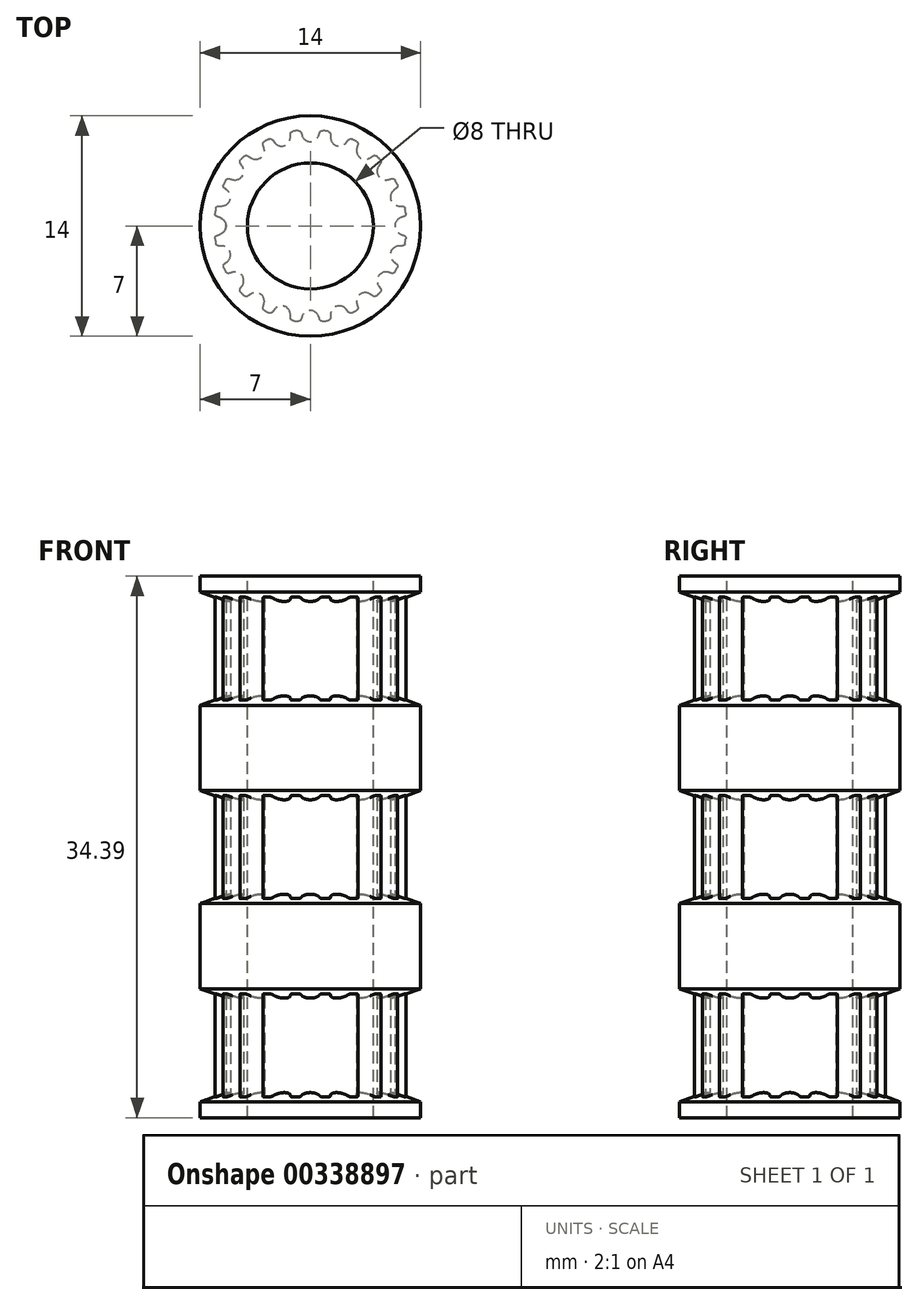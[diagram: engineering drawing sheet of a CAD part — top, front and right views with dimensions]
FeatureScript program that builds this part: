
annotation { "Feature Type Name" : "Feature", "Feature Type Description" : "" }
export const myFeature = defineFeature(function(context is Context, id is Id, definition is map)
    precondition{}
    {
        {
            assignVariable(context, id + "F0", {"name" : "teeth", "anyValue" : 20});
        }
        {
            assignVariable(context, id + "F1", {"name" : "total_length", "anyValue" : 34});
        }
        {
            var Q0;
            Q0=qCreatedBy(makeId("Top.planeOp"),FACE);
            var sketch = newSketch(context, id + "F2", { "sketchPlane" : qUnion([Q0])});
            skLineSegment(sketch, "E0", {"start": v(0, 0) * mm, "end": v(0, 5.36) * mm, "construction": true});
            skCircle(sketch, "E1", {"center": v(0, 0) * mm, "radius": 6.11 * mm});
            skPoint(sketch, "E2.MirrorCS.end.orphan", {"position": v(0.96, 6.04) * mm});
            skLineSegment(sketch, "E3", {"start": v(0.96, 6.04) * mm, "end": v(1, 6.29) * mm, "construction": true});
            skLineSegment(sketch, "E4", {"start": v(-0.96, 6.04) * mm, "end": v(-1, 6.29) * mm, "construction": true});
            skArc(sketch, "E5", {"start": v(0, 5.36) * mm, "mid": v(0.31, 5.46) * mm, "end": v(0.52, 5.72) * mm});
            skArc(sketch, "E6", {"start": v(0.52, 5.72) * mm, "mid": v(0.56, 5.83) * mm, "end": v(0.58, 5.94) * mm, "construction": true});
            skLineSegment(sketch, "E7", {"start": v(0, 5.36) * mm, "end": v(0, 6.11) * mm, "construction": true});
            skLineSegment(sketch, "E8", {"start": v(0, 6.11) * mm, "end": v(0, 6.37) * mm, "construction": true});
            skArc(sketch, "E9", {"start": v(0.58, 5.94) * mm, "mid": v(0.64, 6.04) * mm, "end": v(0.75, 6.07) * mm, "construction": true});
            skArc(sketch, "E10", {"start": v(1, 6.29) * mm, "mid": v(0, 6.37) * mm, "end": v(-1, 6.29) * mm, "construction": true});
            skLineSegment(sketch, "E11", {"start": v(0.96, 6.04) * mm, "end": v(0.84, 5.3) * mm});
            skLineSegment(sketch, "E12", {"start": v(0.84, 5.3) * mm, "end": v(0, 0) * mm});
            skLineSegment(sketch, "E13", {"start": v(0, 0) * mm, "end": v(-0.84, 5.3) * mm});
            skLineSegment(sketch, "E14", {"start": v(-0.84, 5.3) * mm, "end": v(-0.96, 6.04) * mm});
            skArc(sketch, "E15", {"start": v(0.8, 6.06) * mm, "mid": v(0.67, 6.03) * mm, "end": v(0.6, 5.93) * mm});
            skArc(sketch, "E16", {"start": v(0.52, 5.72) * mm, "mid": v(0.56, 5.83) * mm, "end": v(0.6, 5.93) * mm});
            skArc(sketch, "E17.MirrorCS", {"start": v(0, 5.36) * mm, "mid": v(-0.31, 5.46) * mm, "end": v(-0.52, 5.72) * mm});
            skArc(sketch, "E18.MirrorCS", {"start": v(-0.52, 5.72) * mm, "mid": v(-0.56, 5.83) * mm, "end": v(-0.6, 5.93) * mm});
            skArc(sketch, "E19.MirrorCS", {"start": v(-0.8, 6.06) * mm, "mid": v(-0.67, 6.03) * mm, "end": v(-0.6, 5.93) * mm});
            skArc(sketch, "E20", {"start": v(0, 6.11) * mm, "mid": v(-0.2, 6.1) * mm, "end": v(-0.4, 6.1) * mm});
            skArc(sketch, "E21", {"start": v(0.84, 5.3) * mm, "mid": v(0, 5.36) * mm, "end": v(-0.84, 5.3) * mm, "construction": true});
            skLineSegment(sketch, "E22", {"start": v(1, 6.29) * mm, "end": v(1.05, 6.66) * mm, "construction": true});
            skLineSegment(sketch, "E23", {"start": v(-1, 6.29) * mm, "end": v(-1.05, 6.66) * mm, "construction": true});
            skArc(sketch, "E24", {"start": v(-1.05, 6.66) * mm, "mid": v(0, 6.74) * mm, "end": v(1.05, 6.66) * mm, "construction": true});
            skSolve(sketch);
        }
        {
            var Q0;
            Q0=makeQuery(id+"F2.imprint","IMPRINT",FACE,{"disambiguationData":[TD([[makeQuery(id+"F2.imprint","IMPRINT",EDGE,{"derivedFrom":sQuery(id+"F2.wireOp",EDGE,"E5")}),-1.0]])]});
            var Q1;
            {var subQ1=sQuery(id+"F2.wireOp",EDGE,"E14");Q1=makeQuery(id+"F2.imprint","IMPRINT",FACE,{"disambiguationData":[TD([[makeQuery(id+"F2.imprint","IMPRINT",EDGE,{"derivedFrom":subQ1}),-1.0]])]});}
            var Q2;
            {var subQ0=sQuery(id+"F2.wireOp",EDGE,"E12");Q2=makeQuery(id+"F2.imprint","IMPRINT",FACE,{"disambiguationData":[TD([[makeQuery(id+"F2.imprint","IMPRINT",EDGE,{"derivedFrom":subQ0}),-1.0]])]});}
            extrude(context, id + "F3", {"entities" : qUnion([Q0, Q1, Q2]), "endBound" : BoundingType.SYMMETRIC, "depth" : (getVariable(context, 'total_length')) * mm});
        }
        {
            var Q0;
            Q0=makeQuery(id+"F3.opExtrude","SWEPT_BODY",BODY,{"disambiguationData":[OSD([sQuery(id+"F2.wireOp",EDGE,"E1"),sQuery(id+"F2.wireOp",EDGE,"E5"),sQuery(id+"F2.wireOp",EDGE,"E11"),sQuery(id+"F2.wireOp",EDGE,"E12"),sQuery(id+"F2.wireOp",EDGE,"E13"),sQuery(id+"F2.wireOp",EDGE,"E14"),sQuery(id+"F2.wireOp",EDGE,"E15"),sQuery(id+"F2.wireOp",EDGE,"E16"),sQuery(id+"F2.wireOp",EDGE,"E17.MirrorCS"),sQuery(id+"F2.wireOp",EDGE,"E18.MirrorCS"),sQuery(id+"F2.wireOp",EDGE,"E19.MirrorCS")])]});
            var Q1;
            Q1=makeQuery(id+"F3.opExtrude","SWEPT_EDGE",EDGE,{"disambiguationData":[OSD([sQuery(id+"F2.wireOp",EDGE,"E12"),sQuery(id+"F2.wireOp",EDGE,"E13")])]});
            circularPattern(context, id + "F4", {"operationType" : NewBodyOperationType.ADD, "entities" : qUnion([Q0]), "axis" : qUnion([Q1]), "angle" : 360 * degree, "instanceCount" : getVariable(context, 'teeth'), "equalSpace" : true});
        }
        {
            var Q0;
            Q0=qCreatedBy(makeId("Front.planeOp"),FACE);
            var sketch = newSketch(context, id + "F5", { "sketchPlane" : qUnion([Q0])});
            skLineSegment(sketch, "E25", {"start": v(0, 17) * mm, "end": v(7, 17) * mm});
            skLineSegment(sketch, "E26", {"start": v(7, 17) * mm, "end": v(7, 16) * mm});
            skLineSegment(sketch, "E27", {"start": v(7, 16) * mm, "end": v(5.36, 15.4) * mm});
            skLineSegment(sketch, "E28", {"start": v(5.36, 15.4) * mm, "end": v(0, 15.4) * mm});
            skLineSegment(sketch, "E29", {"start": v(0, 15.4) * mm, "end": v(0, 17) * mm});
            skLineSegment(sketch, "E30", {"start": v(0, 9.4) * mm, "end": v(5.36, 9.4) * mm});
            skLineSegment(sketch, "E31", {"start": v(5.36, 9.4) * mm, "end": v(7, 8.8) * mm});
            skLineSegment(sketch, "E32", {"start": v(7, 8.8) * mm, "end": v(7, 3.4) * mm});
            skLineSegment(sketch, "E33", {"start": v(7, 3.4) * mm, "end": v(5.36, 2.8) * mm});
            skLineSegment(sketch, "E34", {"start": v(5.36, 2.8) * mm, "end": v(0, 2.8) * mm});
            skLineSegment(sketch, "E35", {"start": v(0, 2.8) * mm, "end": v(0, 9.4) * mm});
            skLineSegment(sketch, "E36", {"start": v(0, -15.8) * mm, "end": v(5.36, -15.8) * mm});
            skLineSegment(sketch, "E37", {"start": v(5.36, -15.8) * mm, "end": v(7, -16.4) * mm});
            skLineSegment(sketch, "E38", {"start": v(7, -16.4) * mm, "end": v(7, -17.4) * mm});
            skLineSegment(sketch, "E39", {"start": v(7, -17.4) * mm, "end": v(0, -17.4) * mm});
            skLineSegment(sketch, "E40", {"start": v(0, -17.4) * mm, "end": v(0, -15.8) * mm});
            skLineSegment(sketch, "E41", {"start": v(0, -3.2) * mm, "end": v(5.36, -3.2) * mm});
            skLineSegment(sketch, "E42", {"start": v(5.36, -3.2) * mm, "end": v(7, -3.8) * mm});
            skLineSegment(sketch, "E43", {"start": v(7, -3.8) * mm, "end": v(7, -9.2) * mm});
            skLineSegment(sketch, "E44", {"start": v(7, -9.2) * mm, "end": v(5.36, -9.8) * mm});
            skLineSegment(sketch, "E45", {"start": v(5.36, -9.8) * mm, "end": v(0, -9.8) * mm});
            skLineSegment(sketch, "E46", {"start": v(0, -9.8) * mm, "end": v(0, -3.2) * mm});
            skSolve(sketch);
        }
        {
            var Q0;
            Q0=qSketchRegion(id+"F5",true);
            var Q1;
            Q1=sQuery(id+"F5.wireOp",EDGE,"E35");
            revolve(context, id + "F6", {"operationType" : NewBodyOperationType.ADD, "entities" : qUnion([Q0]), "axis" : qUnion([Q1]), "revolveType" : RevolveType.FULL});
        }
        {
            var Q0;
            Q0=qCreatedBy(makeId("Top.planeOp"),FACE);
            var sketch = newSketch(context, id + "F7", { "sketchPlane" : qUnion([Q0])});
            skCircle(sketch, "E47", {"center": v(0, 0) * mm, "radius": 4 * mm});
            skSolve(sketch);
        }
        {
            var Q0;
            Q0=qSketchRegion(id+"F7",true);
            extrude(context, id + "F8", {"entities" : qUnion([Q0]), "operationType" : NewBodyOperationType.REMOVE, "endBound" : BoundingType.SYMMETRIC, "oppositeDirection" : true, "depth" : 100 * mm});
        }
    });
